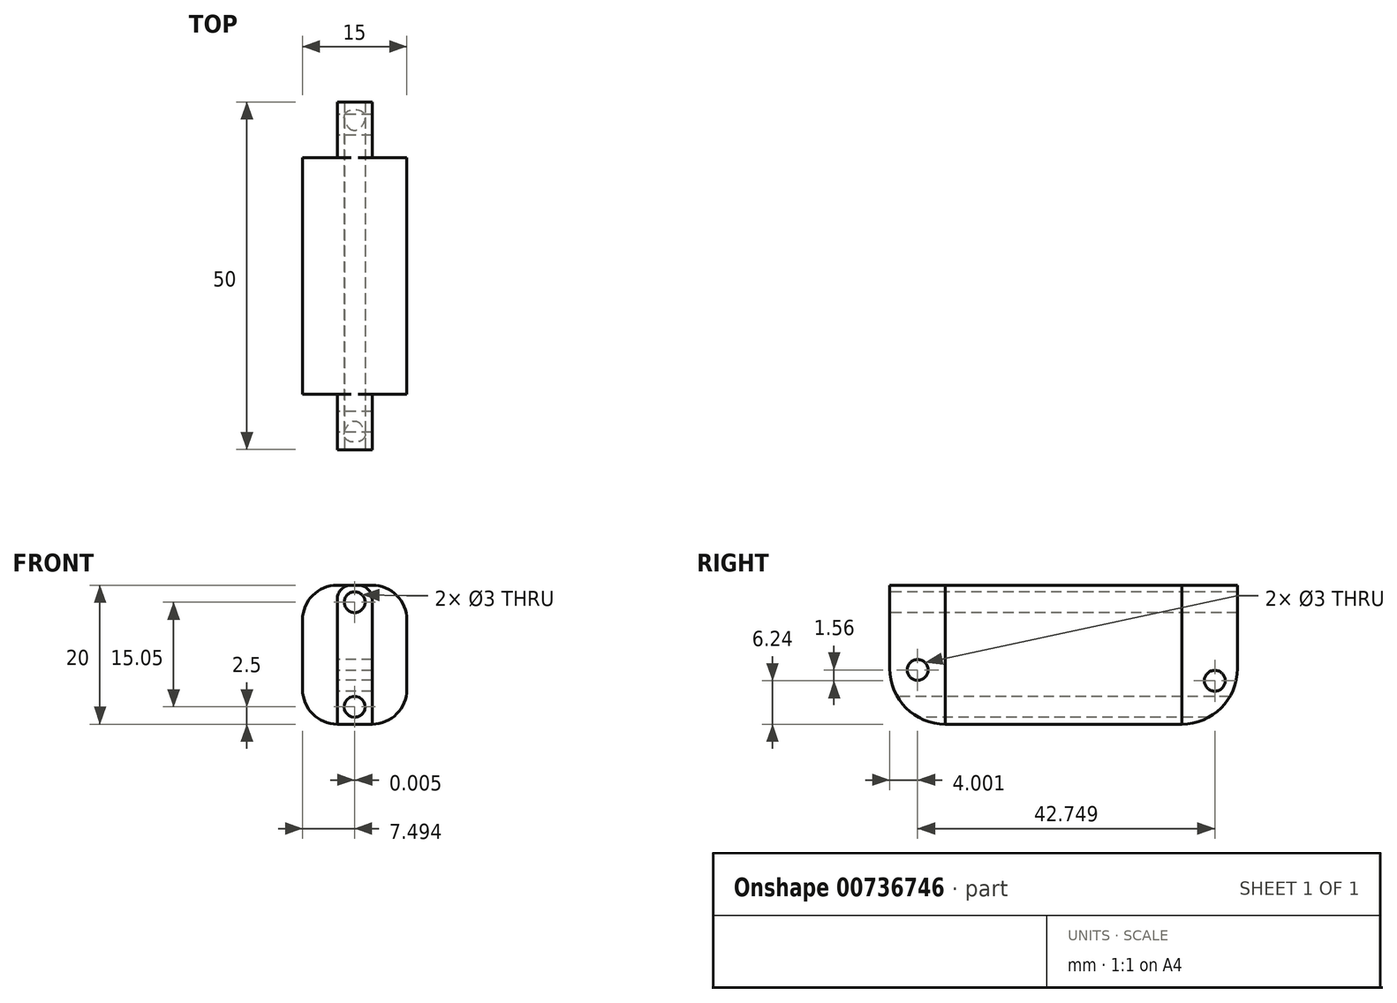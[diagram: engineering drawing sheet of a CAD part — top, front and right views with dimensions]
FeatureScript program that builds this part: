
annotation { "Feature Type Name" : "Feature", "Feature Type Description" : "" }
export const myFeature = defineFeature(function(context is Context, id is Id, definition is map)
    precondition{}
    {
        {
            var Q0;
            Q0=qCreatedBy(makeId("Top.planeOp"),FACE);
            var sketch = newSketch(context, id + "F0", { "sketchPlane" : qUnion([Q0])});
            skLineSegment(sketch, "E0.bottom", {"start": v(23.44, 71.23) * mm, "end": v(38.44, 71.23) * mm});
            skLineSegment(sketch, "E0.top", {"start": v(23.44, 21.23) * mm, "end": v(38.44, 21.23) * mm});
            skLineSegment(sketch, "E0.left", {"start": v(23.44, 71.23) * mm, "end": v(23.44, 21.23) * mm});
            skLineSegment(sketch, "E0.right", {"start": v(38.44, 71.23) * mm, "end": v(38.44, 21.23) * mm});
            skLineSegment(sketch, "E1.bottom", {"start": v(23.44, 71.23) * mm, "end": v(28.44, 71.23) * mm});
            skLineSegment(sketch, "E1.top", {"start": v(23.44, 63.23) * mm, "end": v(28.44, 63.23) * mm});
            skLineSegment(sketch, "E1.left", {"start": v(23.44, 71.23) * mm, "end": v(23.44, 63.23) * mm});
            skLineSegment(sketch, "E1.right", {"start": v(28.44, 71.23) * mm, "end": v(28.44, 63.23) * mm});
            skLineSegment(sketch, "E2.bottom", {"start": v(38.44, 71.23) * mm, "end": v(33.44, 71.23) * mm});
            skLineSegment(sketch, "E2.top", {"start": v(38.44, 63.23) * mm, "end": v(33.44, 63.23) * mm});
            skLineSegment(sketch, "E2.left", {"start": v(38.44, 71.23) * mm, "end": v(38.44, 63.23) * mm});
            skLineSegment(sketch, "E2.right", {"start": v(33.44, 71.23) * mm, "end": v(33.44, 63.23) * mm});
            skLineSegment(sketch, "E3.bottom", {"start": v(23.44, 21.23) * mm, "end": v(28.44, 21.23) * mm});
            skLineSegment(sketch, "E3.top", {"start": v(23.44, 29.23) * mm, "end": v(28.44, 29.23) * mm});
            skLineSegment(sketch, "E3.left", {"start": v(23.44, 21.23) * mm, "end": v(23.44, 29.23) * mm});
            skLineSegment(sketch, "E3.right", {"start": v(28.44, 21.23) * mm, "end": v(28.44, 29.23) * mm});
            skLineSegment(sketch, "E4.bottom", {"start": v(38.44, 21.23) * mm, "end": v(33.44, 21.23) * mm});
            skLineSegment(sketch, "E4.top", {"start": v(38.44, 29.23) * mm, "end": v(33.44, 29.23) * mm});
            skLineSegment(sketch, "E4.left", {"start": v(38.44, 21.23) * mm, "end": v(38.44, 29.23) * mm});
            skLineSegment(sketch, "E4.right", {"start": v(33.44, 21.23) * mm, "end": v(33.44, 29.23) * mm});
            skSolve(sketch);
        }
        {
            var Q0;
            {var subQ2=sQuery(id+"F0.wireOp",EDGE,"E1.top");Q0=makeQuery(id+"F0.imprint","IMPRINT",FACE,{"disambiguationData":[TD([[makeQuery(id+"F0.imprint","IMPRINT",EDGE,{"derivedFrom":subQ2}),-1.0]])]});}
            extrude(context, id + "F1", {"entities" : qUnion([Q0]), "depth" : 20 * mm, "offsetDistance" : 25 * mm});
        }
        {
            var Q0;
            Q0=makeQuery(id+"F1.opExtrude","CAP_EDGE",EDGE,{"disambiguationData":[OSD([sQuery(id+"F0.wireOp",EDGE,"E0.top")])],"isStart":true});
            var Q1;
            Q1=makeQuery(id+"F1.opExtrude","CAP_EDGE",EDGE,{"disambiguationData":[OSD([sQuery(id+"F0.wireOp",EDGE,"E0.bottom")])],"isStart":true});
            fillet(context, id + "F2", {"entities" : qUnion([Q0, Q1]), "radius" : 8 * mm, "tangentPropagation" : true, "allowEdgeOverflow" : false});
        }
        {
            var Q0;
            Q0=makeQuery(id+"F1.opExtrude","CAP_EDGE",EDGE,{"disambiguationData":[OSD([sQuery(id+"F0.wireOp",EDGE,"E0.right")])],"isStart":false});
            var Q1;
            Q1=makeQuery(id+"F1.opExtrude","CAP_EDGE",EDGE,{"disambiguationData":[OSD([sQuery(id+"F0.wireOp",EDGE,"E0.left")])],"isStart":false});
            var Q2;
            Q2=makeQuery(id+"F1.opExtrude","CAP_EDGE",EDGE,{"disambiguationData":[OSD([sQuery(id+"F0.wireOp",EDGE,"E0.right")])],"isStart":true});
            var Q3;
            Q3=makeQuery(id+"F1.opExtrude","CAP_EDGE",EDGE,{"disambiguationData":[OSD([sQuery(id+"F0.wireOp",EDGE,"E0.left")])],"isStart":true});
            fillet(context, id + "F3", {"entities" : qUnion([Q0, Q1, Q2, Q3]), "radius" : 5 * mm, "tangentPropagation" : true, "allowEdgeOverflow" : false});
        }
        {
            var Q0;
            Q0=makeQuery(id+"F1.opExtrude","CAP_EDGE",EDGE,{"disambiguationData":[OSD([sQuery(id+"F0.wireOp",EDGE,"E4.right")])],"isStart":false});
            var Q1;
            Q1=makeQuery(id+"F1.opExtrude","CAP_EDGE",EDGE,{"disambiguationData":[OSD([sQuery(id+"F0.wireOp",EDGE,"E2.right")])],"isStart":false});
            var Q2;
            Q2=makeQuery(id+"F1.opExtrude","CAP_EDGE",EDGE,{"disambiguationData":[OSD([sQuery(id+"F0.wireOp",EDGE,"E1.right")])],"isStart":false});
            var Q3;
            Q3=makeQuery(id+"F1.opExtrude","CAP_EDGE",EDGE,{"disambiguationData":[OSD([sQuery(id+"F0.wireOp",EDGE,"E3.right")])],"isStart":false});
            fillet(context, id + "F4", {"entities" : qUnion([Q0, Q1, Q2, Q3]), "radius" : 2 * mm, "tangentPropagation" : true, "allowEdgeOverflow" : false});
        }
        {
            var Q0;
            Q0=qCreatedBy(makeId("Right.planeOp"),FACE);
            var sketch = newSketch(context, id + "F5", { "sketchPlane" : qUnion([Q0])});
            skCircle(sketch, "E5", {"center": v(25.23, 7.8) * mm, "radius": 1.5 * mm});
            skCircle(sketch, "E6", {"center": v(67.98, 6.24) * mm, "radius": 1.5 * mm});
            skSolve(sketch);
        }
        {
            var Q0;
            Q0=makeQuery(id+"F5.imprint","IMPRINT",FACE,{"disambiguationData":[TD([[makeQuery(id+"F5.imprint","IMPRINT",EDGE,{"derivedFrom":sQuery(id+"F5.wireOp",EDGE,"E6")}),1.0]])]});
            var Q1;
            Q1=makeQuery(id+"F5.imprint","IMPRINT",FACE,{"disambiguationData":[TD([[makeQuery(id+"F5.imprint","IMPRINT",EDGE,{"derivedFrom":sQuery(id+"F5.wireOp",EDGE,"E5")}),1.0]])]});
            extrude(context, id + "F6", {"entities" : qUnion([Q0, Q1]), "operationType" : NewBodyOperationType.REMOVE, "depth" : 50 * mm, "offsetDistance" : 25 * mm});
        }
        {
            var Q0;
            Q0=qCreatedBy(makeId("Front.planeOp"),FACE);
            var sketch = newSketch(context, id + "F7", { "sketchPlane" : qUnion([Q0])});
            skCircle(sketch, "E7", {"center": v(30.94, 17.55) * mm, "radius": 1.5 * mm});
            skCircle(sketch, "E8", {"center": v(30.93, 2.5) * mm, "radius": 1.5 * mm});
            skSolve(sketch);
        }
        {
            var Q0;
            Q0=makeQuery(id+"F7.imprint","IMPRINT",FACE,{"disambiguationData":[TD([[makeQuery(id+"F7.imprint","IMPRINT",EDGE,{"derivedFrom":sQuery(id+"F7.wireOp",EDGE,"E7")}),1.0]])]});
            var Q1;
            Q1=makeQuery(id+"F7.imprint","IMPRINT",FACE,{"disambiguationData":[TD([[makeQuery(id+"F7.imprint","IMPRINT",EDGE,{"derivedFrom":sQuery(id+"F7.wireOp",EDGE,"E8")}),1.0]])]});
            extrude(context, id + "F8", {"entities" : qUnion([Q0, Q1]), "operationType" : NewBodyOperationType.REMOVE, "oppositeDirection" : true, "depth" : 82.9 * mm, "offsetDistance" : 25 * mm});
        }
    });
